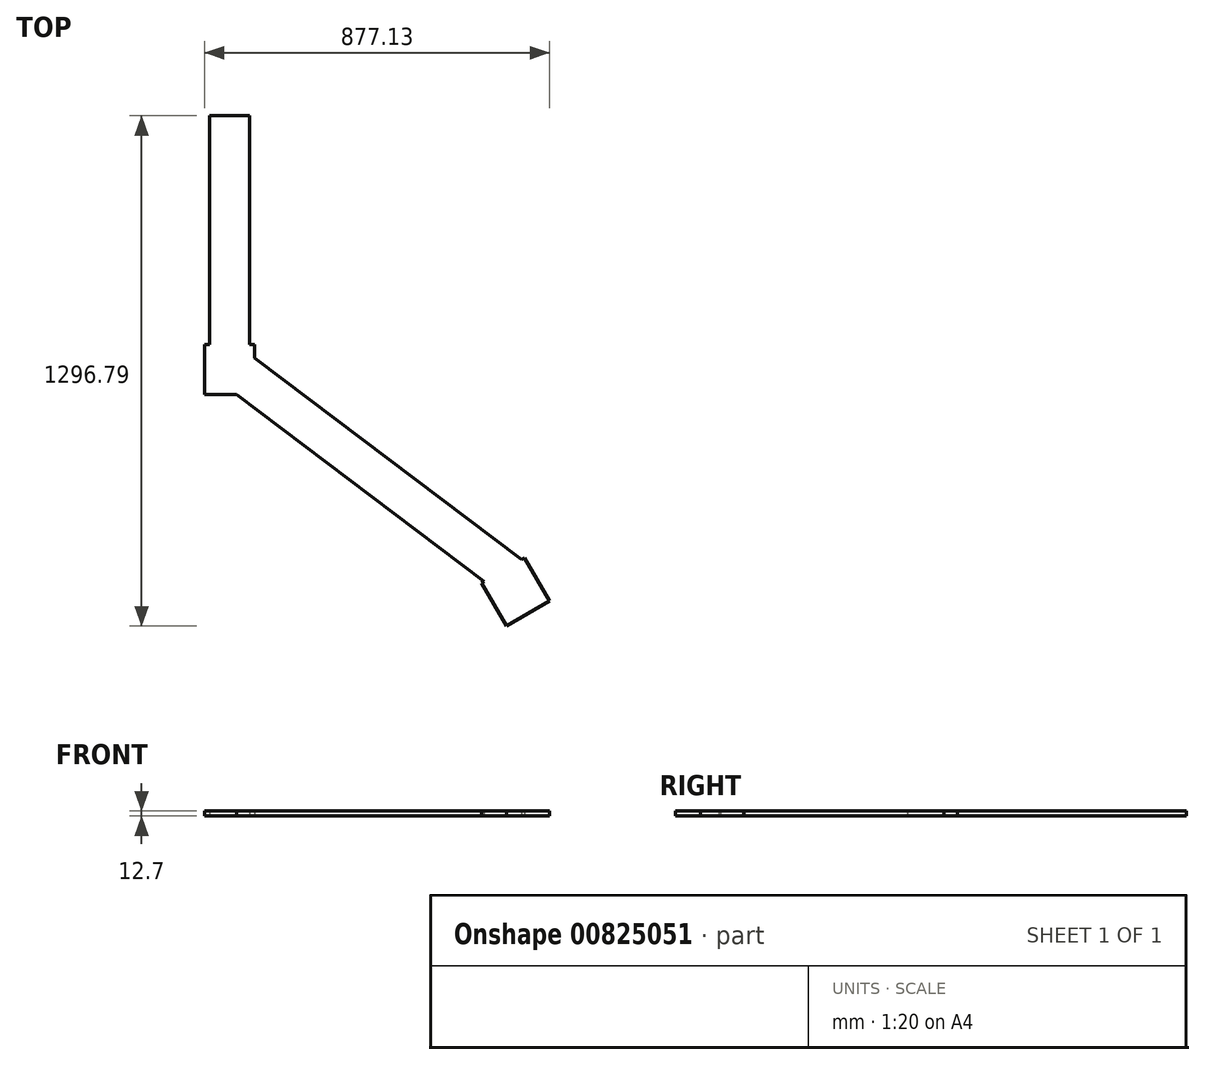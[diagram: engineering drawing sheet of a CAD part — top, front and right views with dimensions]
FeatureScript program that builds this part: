
annotation { "Feature Type Name" : "Feature", "Feature Type Description" : "" }
export const myFeature = defineFeature(function(context is Context, id is Id, definition is map)
    precondition{}
    {
        {
            var Q0;
            Q0=qCreatedBy(makeId("Top.planeOp"),FACE);
            var sketch = newSketch(context, id + "F0", { "sketchPlane" : qUnion([Q0])});
            skLineSegment(sketch, "E0", {"start": v(-287.35, 764.68) * mm, "end": v(-287.35, 183.1) * mm});
            skLineSegment(sketch, "E1", {"start": v(-287.35, 183.1) * mm, "end": v(-185.75, 183.1) * mm});
            skLineSegment(sketch, "E2", {"start": v(-185.75, 183.1) * mm, "end": v(-185.75, 764.68) * mm});
            skLineSegment(sketch, "E3.bottom", {"start": v(-300.05, 183.1) * mm, "end": v(-173.05, 183.1) * mm});
            skLineSegment(sketch, "E3.top", {"start": v(-300.05, 56.1) * mm, "end": v(-218.2, 56.1) * mm});
            skLineSegment(sketch, "E3.left", {"start": v(-300.05, 183.1) * mm, "end": v(-300.05, 56.1) * mm});
            skLineSegment(sketch, "E3.right", {"start": v(-173.05, 183.1) * mm, "end": v(-173.05, 149.3) * mm});
            skLineSegment(sketch, "E4", {"start": v(513.58, -358.62) * mm, "end": v(403.6, -422.12) * mm});
            skLineSegment(sketch, "E5", {"start": v(403.6, -422.12) * mm, "end": v(467.1, -532.1) * mm});
            skLineSegment(sketch, "E6", {"start": v(467.1, -532.1) * mm, "end": v(577.08, -468.6) * mm});
            skLineSegment(sketch, "E7", {"start": v(-173.05, 149.3) * mm, "end": v(505.82, -363.1) * mm});
            skLineSegment(sketch, "E8", {"start": v(-218.2, 56.1) * mm, "end": v(410.26, -418.27) * mm});
            skLineSegment(sketch, "E9", {"start": v(-287.35, 764.68) * mm, "end": v(-185.75, 764.68) * mm});
            skLineSegment(sketch, "E10", {"start": v(513.58, -358.62) * mm, "end": v(577.08, -468.6) * mm});
            skSolve(sketch);
        }
        {
            var Q0;
            {var subQ0=sQuery(id+"F0.wireOp",EDGE,"E0");Q0=makeQuery(id+"F0.imprint","IMPRINT",FACE,{"disambiguationData":[TD([[makeQuery(id+"F0.imprint","IMPRINT",EDGE,{"derivedFrom":subQ0}),1.0]])]});}
            var Q1;
            Q1=makeQuery(id+"F0.imprint","IMPRINT",FACE,{"disambiguationData":[TD([[makeQuery(id+"F0.imprint","IMPRINT",EDGE,{"derivedFrom":sQuery(id+"F0.wireOp",EDGE,"E3.top")}),1.0]])]});
            var Q2;
            {var subQ0=sQuery(id+"F0.wireOp",EDGE,"E5");Q2=makeQuery(id+"F0.imprint","IMPRINT",FACE,{"disambiguationData":[TD([[makeQuery(id+"F0.imprint","IMPRINT",EDGE,{"derivedFrom":subQ0}),1.0]])]});}
            extrude(context, id + "F1", {"entities" : qUnion([Q0, Q1, Q2]), "depth" : 12.7 * mm, "offsetDistance" : 25.4 * mm});
        }
    });
